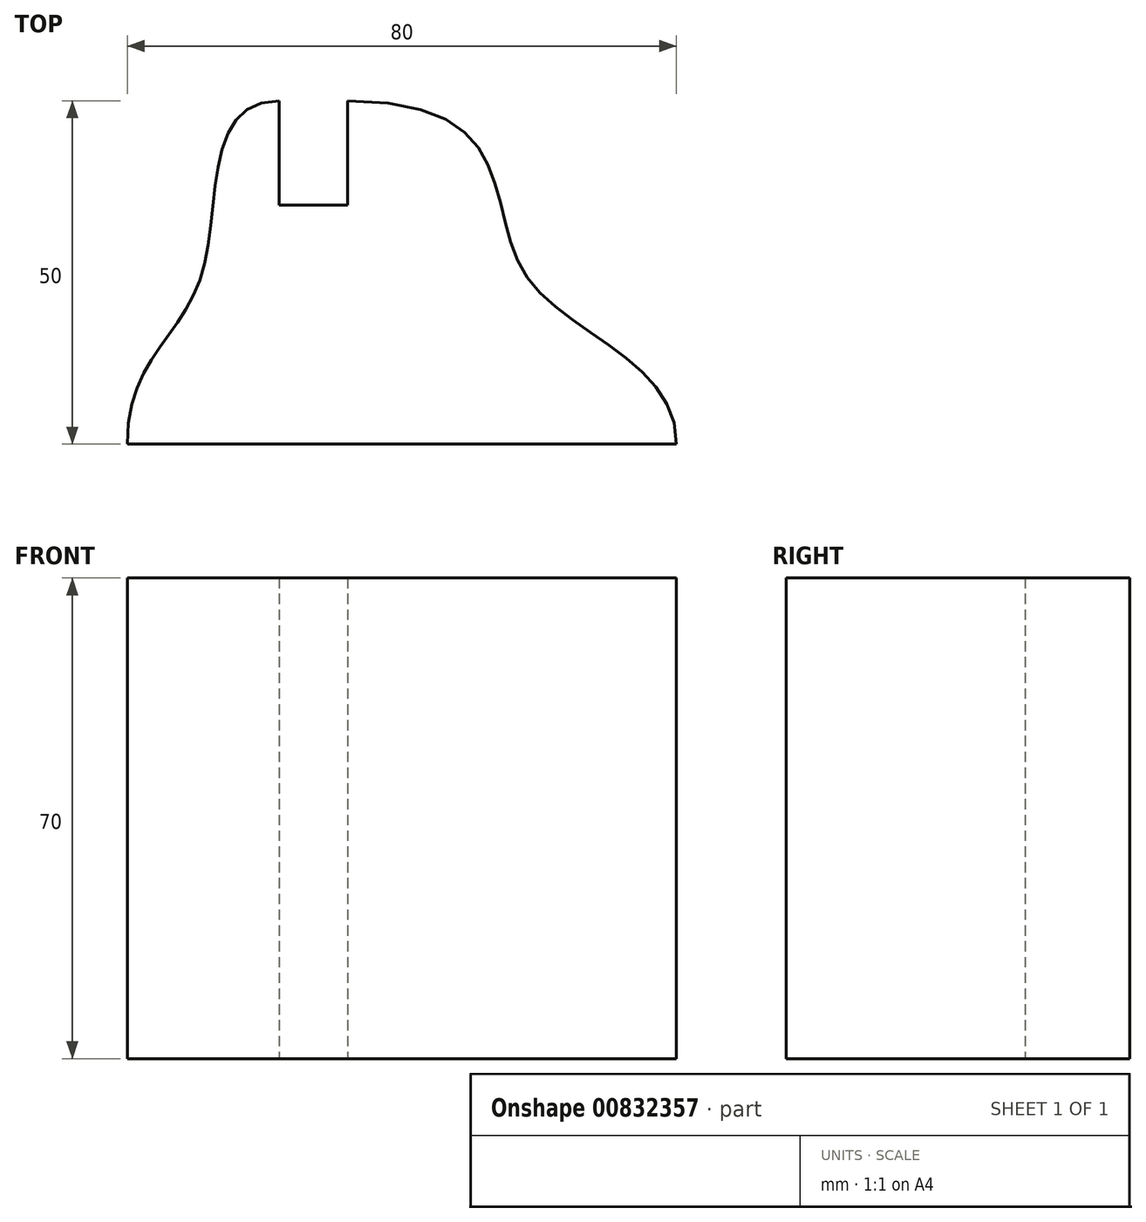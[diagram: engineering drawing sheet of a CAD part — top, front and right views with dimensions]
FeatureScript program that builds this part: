
annotation { "Feature Type Name" : "Feature", "Feature Type Description" : "" }
export const myFeature = defineFeature(function(context is Context, id is Id, definition is map)
    precondition{}
    {
        {
            var Q0;
            Q0=qCreatedBy(makeId("Top.planeOp"),FACE);
            var sketch = newSketch(context, id + "F0", { "sketchPlane" : qUnion([Q0])});
            skLineSegment(sketch, "E0", {"start": v(0, -25) * mm, "end": v(47.9, -25) * mm});
            skLineSegment(sketch, "E1", {"start": v(0, -25) * mm, "end": v(-32.1, -25) * mm});
            skFitSpline(sketch, "E2", {"points": [v(-10, 25) * mm, v(-21.18, 0) * mm, v(-32.1, -25) * mm], "startDerivative": vector(-67.02, 0) * mm, "endDerivative": vector(0, -75.07) * mm});
            skLineSegment(sketch, "E3", {"start": v(-10, 25) * mm, "end": v(-10, 9.8) * mm});
            skLineSegment(sketch, "E4", {"start": v(-10, 9.8) * mm, "end": v(0, 9.8) * mm});
            skLineSegment(sketch, "E5", {"start": v(0, 9.8) * mm, "end": v(0, 25) * mm});
            skFitSpline(sketch, "E6", {"points": [v(0, 25) * mm, v(25.66, 0) * mm, v(47.9, -25) * mm], "startDerivative": vector(151.37, 0) * mm, "endDerivative": vector(0, -76.3) * mm});
            skSolve(sketch);
        }
        {
            var Q0;
            Q0=makeQuery(id+"F0.imprint","IMPRINT",FACE,{"disambiguationData":[TD([[makeQuery(id+"F0.imprint","IMPRINT",EDGE,{"derivedFrom":sQuery(id+"F0.wireOp",EDGE,"E0")}),1.0]])]});
            extrude(context, id + "F1", {"entities" : qUnion([Q0]), "depth" : 70 * mm, "offsetDistance" : 25 * mm});
        }
    });
